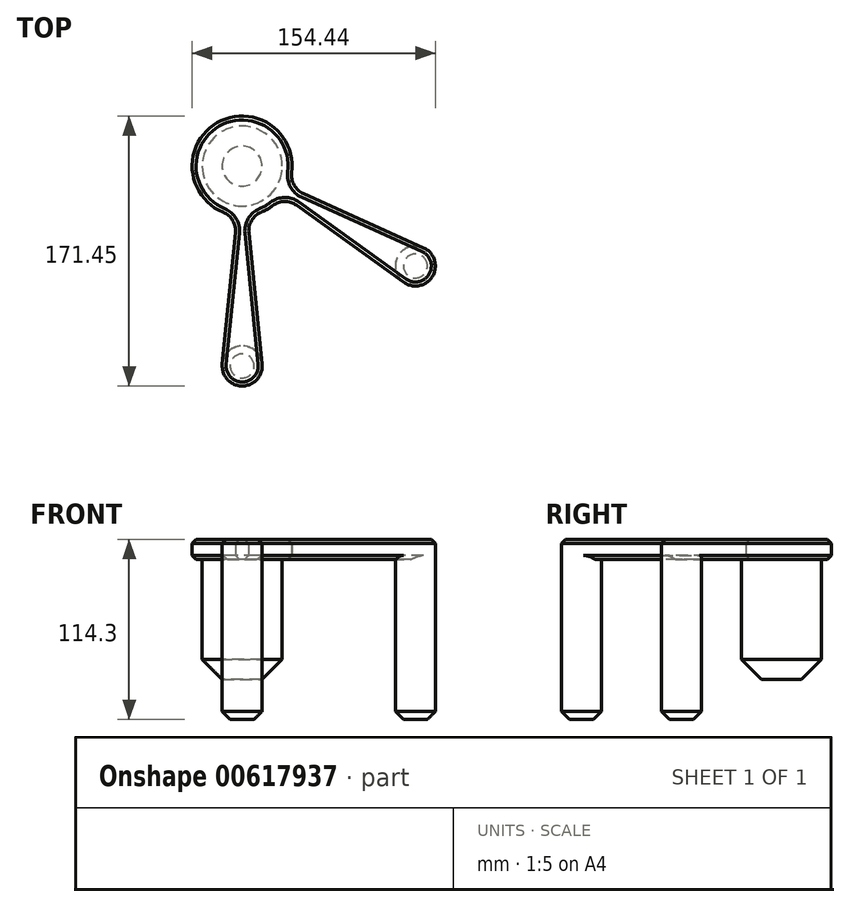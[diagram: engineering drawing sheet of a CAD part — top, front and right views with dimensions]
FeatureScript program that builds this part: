
annotation { "Feature Type Name" : "Feature", "Feature Type Description" : "" }
export const myFeature = defineFeature(function(context is Context, id is Id, definition is map)
    precondition{}
    {
        {
            var Q0;
            Q0=qCreatedBy(makeId("Top.planeOp"),FACE);
            var sketch = newSketch(context, id + "F0", { "sketchPlane" : qUnion([Q0])});
            skCircle(sketch, "E0", {"center": v(0, 0) * mm, "radius": 31.75 * mm});
            skCircle(sketch, "E1", {"center": v(0, -127) * mm, "radius": 12.7 * mm});
            skCircle(sketch, "E2", {"center": v(109.99, -63.5) * mm, "radius": 12.7 * mm});
            skLineSegment(sketch, "E3", {"start": v(0, 0) * mm, "end": v(0, -127) * mm});
            skLineSegment(sketch, "E4", {"start": v(0, 0) * mm, "end": v(109.99, -63.5) * mm});
            skLineSegment(sketch, "E5", {"start": v(0, 0) * mm, "end": v(-12.64, -125.73) * mm});
            skLineSegment(sketch, "E6", {"start": v(0, 0) * mm, "end": v(12.64, -125.73) * mm});
            skLineSegment(sketch, "E7", {"start": v(0, 0) * mm, "end": v(102.57, -73.8) * mm});
            skLineSegment(sketch, "E8", {"start": v(0, 0) * mm, "end": v(115.2, -51.92) * mm});
            skSolve(sketch);
        }
        {
            var Q0;
            Q0 = qSketchRegion(id + "F0", true);
            extrude(context, id + "F1", {"entities" : qUnion([Q0]), "depth" : 12.7 * mm, "offsetDistance" : 25.4 * mm});
        }
        {
            var Q0;
            {var subQ0=sQuery(id+"F0.wireOp",EDGE,"E2");var subQ1=makeQuery(id+"F0.imprint","INTERSECT",VERTEX,{"derivedFrom":[subQ0,sQuery(id+"F0.wireOp",EDGE,"E8")]});Q0=makeQuery(id+"F0.imprint","IMPRINT",FACE,{"disambiguationData":[TD([[makeQuery(id+"F0.imprint","IMPRINT",EDGE,{"disambiguationData":[TD([[subQ1,-1.0]])],"derivedFrom":subQ0}),1.0]])]});}
            var Q1;
            {var subQ0=sQuery(id+"F0.wireOp",EDGE,"E1");var subQ1=makeQuery(id+"F0.imprint","INTERSECT",VERTEX,{"derivedFrom":[subQ0,sQuery(id+"F0.wireOp",EDGE,"E6")]});Q1=makeQuery(id+"F0.imprint","IMPRINT",FACE,{"disambiguationData":[TD([[makeQuery(id+"F0.imprint","IMPRINT",EDGE,{"disambiguationData":[TD([[subQ1,-1.0]])],"derivedFrom":subQ0}),1.0]])]});}
            extrude(context, id + "F2", {"entities" : qUnion([Q0, Q1]), "operationType" : NewBodyOperationType.ADD, "oppositeDirection" : true, "depth" : 101.6 * mm, "offsetDistance" : 25.4 * mm});
        }
        {
            var Q0;
            Q0=makeQuery(id+"F1.opExtrude","SWEPT_EDGE",EDGE,{"disambiguationData":[OSD([sQuery(id+"F0.wireOp",EDGE,"E0"),sQuery(id+"F0.wireOp",EDGE,"E5")])]});
            var Q1;
            Q1=makeQuery(id+"F1.opExtrude","SWEPT_EDGE",EDGE,{"disambiguationData":[OSD([sQuery(id+"F0.wireOp",EDGE,"E0"),sQuery(id+"F0.wireOp",EDGE,"E6")])]});
            var Q2;
            Q2=makeQuery(id+"F1.opExtrude","SWEPT_EDGE",EDGE,{"disambiguationData":[OSD([sQuery(id+"F0.wireOp",EDGE,"E0"),sQuery(id+"F0.wireOp",EDGE,"E7")])]});
            var Q3;
            Q3=makeQuery(id+"F1.opExtrude","SWEPT_EDGE",EDGE,{"disambiguationData":[OSD([sQuery(id+"F0.wireOp",EDGE,"E0"),sQuery(id+"F0.wireOp",EDGE,"E8")])]});
            fillet(context, id + "F3", {"entities" : qUnion([Q0, Q1, Q2, Q3]), "radius" : 12.7 * mm, "tangentPropagation" : true, "allowEdgeOverflow" : false});
        }
        {
            var Q0;
            Q0=makeQuery(id+"F1.opExtrude","CAP_FACE",FACE,{"disambiguationData":[OSD([sQuery(id+"F0.wireOp",EDGE,"E0"),sQuery(id+"F0.wireOp",EDGE,"E1"),sQuery(id+"F0.wireOp",EDGE,"E2"),sQuery(id+"F0.wireOp",EDGE,"E5"),sQuery(id+"F0.wireOp",EDGE,"E6"),sQuery(id+"F0.wireOp",EDGE,"E7"),sQuery(id+"F0.wireOp",EDGE,"E8")])],"isStart":true});
            var sketch = newSketch(context, id + "F4", { "sketchPlane" : qUnion([Q0])});
            skCircle(sketch, "E9", {"center": v(0, 0) * mm, "radius": 25.4 * mm});
            skSolve(sketch);
        }
        {
            var Q0;
            Q0 = qSketchRegion(id + "F4", true);
            extrude(context, id + "F5", {"entities" : qUnion([Q0]), "operationType" : NewBodyOperationType.ADD, "depth" : 76.2 * mm, "offsetDistance" : 25.4 * mm});
        }
        {
            var Q0;
            Q0=makeQuery(id+"F5.opExtrude","CAP_EDGE",EDGE,{"disambiguationData":[OSD([sQuery(id+"F4.wireOp",EDGE,"E9")])],"isStart":false});
            chamfer(context, id + "F6", {"entities" : qUnion([Q0]), "width" : 12.7 * mm, "tangentPropagation" : true});
        }
        {
            var Q0;
            Q0=makeQuery(id+"F1.opExtrude","CAP_FACE",FACE,{"disambiguationData":[OSD([sQuery(id+"F0.wireOp",EDGE,"E0"),sQuery(id+"F0.wireOp",EDGE,"E1"),sQuery(id+"F0.wireOp",EDGE,"E2"),sQuery(id+"F0.wireOp",EDGE,"E5"),sQuery(id+"F0.wireOp",EDGE,"E6"),sQuery(id+"F0.wireOp",EDGE,"E7"),sQuery(id+"F0.wireOp",EDGE,"E8")])],"isStart":false});
            chamfer(context, id + "F7", {"entities" : qUnion([Q0]), "width" : 2.54 * mm, "tangentPropagation" : true});
        }
        {
            var Q0;
            Q0=makeQuery(id+"F2.opExtrude","CAP_EDGE",EDGE,{"disambiguationData":[OSD([sQuery(id+"F0.wireOp",EDGE,"E1")])],"isStart":false});
            var Q1;
            Q1=makeQuery(id+"F2.opExtrude","CAP_EDGE",EDGE,{"disambiguationData":[OSD([sQuery(id+"F0.wireOp",EDGE,"E2")])],"isStart":false});
            chamfer(context, id + "F8", {"entities" : qUnion([Q0, Q1]), "width" : 5.08 * mm, "tangentPropagation" : true});
        }
        {
            var Q0;
            {var subQ0=sQuery(id+"F0.wireOp",EDGE,"E0");Q0=makeQuery(id+"F1.opExtrude","CAP_EDGE",EDGE,{"disambiguationData":[OSD([subQ0]),TDD([makeQuery(id+"F0.imprint","IMPRINT",EDGE,{"disambiguationData":[TD([[makeQuery(id+"F0.imprint","INTERSECT",VERTEX,{"derivedFrom":[subQ0,sQuery(id+"F0.wireOp",EDGE,"E5")]}),1.0]])],"derivedFrom":subQ0})])],"isStart":true});}
            var Q1;
            Q1=makeQuery(id+"F1.opExtrude","CAP_EDGE",EDGE,{"disambiguationData":[OSD([sQuery(id+"F0.wireOp",EDGE,"E7")])],"isStart":true});
            chamfer(context, id + "F9", {"entities" : qUnion([Q0, Q1]), "width" : 2.54 * mm, "tangentPropagation" : true});
        }
    });
